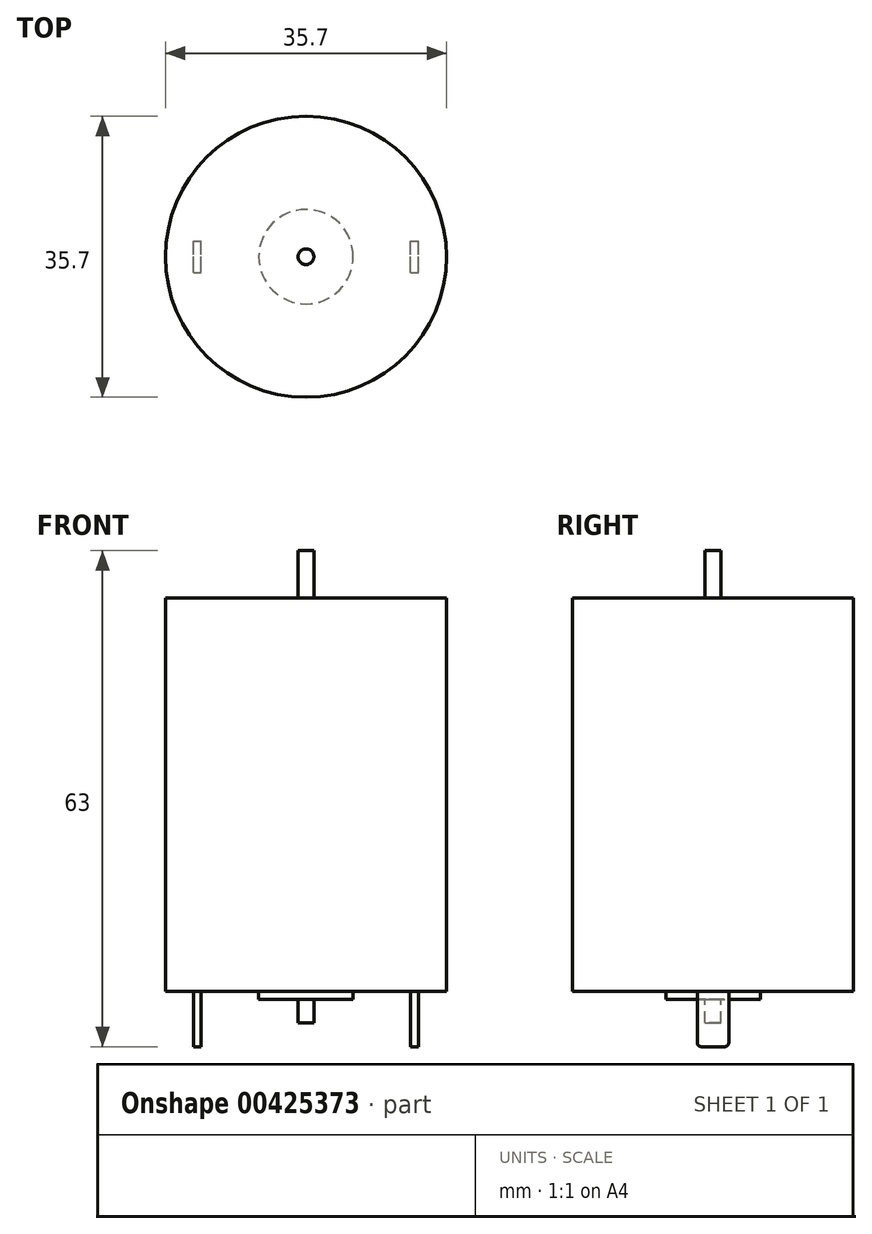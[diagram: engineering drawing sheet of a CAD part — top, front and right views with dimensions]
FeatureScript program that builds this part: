
annotation { "Feature Type Name" : "Feature", "Feature Type Description" : "" }
export const myFeature = defineFeature(function(context is Context, id is Id, definition is map)
    precondition{}
    {
        {
            var Q0;
            Q0=qCreatedBy(makeId("Top.planeOp"),FACE);
            var sketch = newSketch(context, id + "F0", { "sketchPlane" : qUnion([Q0])});
            skCircle(sketch, "E0", {"center": v(0, 0) * mm, "radius": 17.85 * mm});
            skSolve(sketch);
        }
        {
            var Q0;
            Q0 = qSketchRegion(id + "F0", true);
            extrude(context, id + "F1", {"entities" : qUnion([Q0]), "depth" : 50 * mm});
        }
        {
            var Q0;
            Q0=qCreatedBy(makeId("Top.planeOp"),FACE);
            var sketch = newSketch(context, id + "F2", { "sketchPlane" : qUnion([Q0])});
            skCircle(sketch, "E1", {"center": v(0, 0) * mm, "radius": 1 * mm});
            skSolve(sketch);
        }
        {
            var Q0;
            Q0 = qSketchRegion(id + "F2", true);
            extrude(context, id + "F3", {"entities" : qUnion([Q0]), "operationType" : NewBodyOperationType.ADD, "oppositeDirection" : true, "depth" : 4 * mm, "hasSecondDirection" : true, "secondDirectionOppositeDirection" : false, "secondDirectionDepth" : 56 * mm});
        }
        {
            var Q0;
            Q0=qCreatedBy(makeId("Top.planeOp"),FACE);
            var sketch = newSketch(context, id + "F4", { "sketchPlane" : qUnion([Q0])});
            skCircle(sketch, "E2", {"center": v(0, 0) * mm, "radius": 6 * mm});
            skSolve(sketch);
        }
        {
            var Q0;
            Q0 = qSketchRegion(id + "F4", true);
            extrude(context, id + "F5", {"entities" : qUnion([Q0]), "operationType" : NewBodyOperationType.ADD, "oppositeDirection" : true, "depth" : 1 * mm});
        }
        {
            var Q0;
            Q0=qCreatedBy(makeId("Top.planeOp"),FACE);
            var sketch = newSketch(context, id + "F6", { "sketchPlane" : qUnion([Q0])});
            skLineSegment(sketch, "E3.bottom", {"start": v(-14.3, -2) * mm, "end": v(-13.3, -2) * mm});
            skLineSegment(sketch, "E3.top", {"start": v(-14.3, 2) * mm, "end": v(-13.3, 2) * mm});
            skLineSegment(sketch, "E3.left", {"start": v(-14.3, -2) * mm, "end": v(-14.3, 2) * mm});
            skLineSegment(sketch, "E3.right", {"start": v(-13.3, -2) * mm, "end": v(-13.3, 2) * mm});
            skLineSegment(sketch, "E4.bottom", {"start": v(13.3, -2) * mm, "end": v(14.3, -2) * mm});
            skLineSegment(sketch, "E4.top", {"start": v(13.3, 2) * mm, "end": v(14.3, 2) * mm});
            skLineSegment(sketch, "E4.left", {"start": v(13.3, -2) * mm, "end": v(13.3, 2) * mm});
            skLineSegment(sketch, "E4.right", {"start": v(14.3, -2) * mm, "end": v(14.3, 2) * mm});
            skSolve(sketch);
        }
        {
            var Q0;
            Q0 = qSketchRegion(id + "F6", true);
            extrude(context, id + "F7", {"entities" : qUnion([Q0]), "operationType" : NewBodyOperationType.ADD, "oppositeDirection" : true, "depth" : 7 * mm});
        }
        {
            var Q0;
            Q0=makeQuery(id+"F7.opExtrude","CAP_EDGE",EDGE,{"disambiguationData":[OSD([sQuery(id+"F6.wireOp",EDGE,"E4.bottom")])],"isStart":false});
            var Q1;
            Q1=makeQuery(id+"F7.opExtrude","CAP_EDGE",EDGE,{"disambiguationData":[OSD([sQuery(id+"F6.wireOp",EDGE,"E3.bottom")])],"isStart":false});
            var Q2;
            Q2=makeQuery(id+"F7.opExtrude","CAP_EDGE",EDGE,{"disambiguationData":[OSD([sQuery(id+"F6.wireOp",EDGE,"E3.top")])],"isStart":false});
            var Q3;
            Q3=makeQuery(id+"F7.opExtrude","CAP_EDGE",EDGE,{"disambiguationData":[OSD([sQuery(id+"F6.wireOp",EDGE,"E4.top")])],"isStart":false});
            fillet(context, id + "F8", {"entities" : qUnion([Q0, Q1, Q2, Q3]), "radius" : 0.5 * mm, "tangentPropagation" : true, "allowEdgeOverflow" : false});
        }
    });
